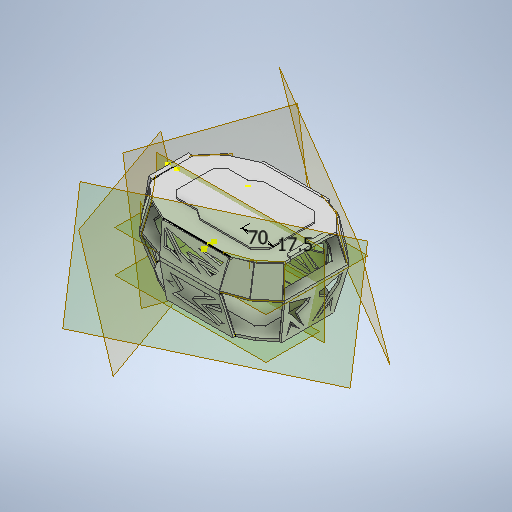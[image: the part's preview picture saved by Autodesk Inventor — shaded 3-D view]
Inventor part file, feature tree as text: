
AUTODESK INVENTOR PART (.ipt)
format: ipt  version: 2025.2 (Build 292293000, 293)  size: 6,053,888 bytes
history: native  units: mm
features: sketch x43, extrude x34, other x23, plane x17, loft x11, mirror x2
ambient origin geometry x8: Origin, YZ Plane, XZ Plane, XY Plane, X Axis, Y Axis, Z Axis, Center Point
bodies: Body1 (feature_tree)
feature tree (130):
  extrude  "Extrusion2"  Depth=45.0mm
  extrude  "Extrusion3"  Depth=40.0mm
  plane  "Work Plane3"
  extrude  "Extrusion4"  Depth=145.0mm
  extrude  "Extrusion5"  Depth=55.0mm
  plane  "Work Plane4"
  extrude  "Extrusion6"  Depth=40.0mm
  sketch  "Sketch8"  dims[d17=165.0deg d18=15.0mm]
  sketch  "Sketch9"  dims[d20=10.0mm d21=40.0mm]
  sketch  "Sketch10"  dims[d22=5.0mm d23=5.0mm]
  loft  "Loft1"
  loft  "Loft2"
  extrude  "Extrusion7"  Depth=5.0mm
  extrude  "Extrusion8"  TaperAngle=90.0deg  [1 undecoded]
  extrude  "Extrusion9"  Depth=30.0mm
  sketch  "Sketch14"  dims[d30=45.0mm d31=20.0mm]
  sketch  "Sketch15"  dims[d32=45.0deg d39=5.0mm d40=0.0mm]
  sketch  "Sketch16"  dims[d41=3.0mm d42=3.0mm d43=0.0mm d44=0.0mm d45=150.0mm]
  loft  "Loft3"
  loft  "Loft4"
  loft  "Loft5"
  extrude  "Extrusion10"  Depth=3.0mm
  extrude  "Extrusion11"  Depth=10.0mm
  extrude  "Extrusion12"  Depth=10.0mm
  extrude  "Extrusion13"  Depth=10.0mm
  extrude  "Extrusion14"  Depth=10.0mm
  loft  "Loft7"
  loft  "Loft8"
  sketch  "Sketch22"  dims[d57=10.0mm d58=10.0mm]
  plane  "Work Plane5"
  extrude  "Extrusion15"  Depth=3.0mm TaperAngle=0.0deg
  plane  "Work Plane6"
  extrude  "Extrusion16"  Depth=10.0mm
  extrude  "Extrusion17"  Depth=50.0mm
  plane  "Work Plane7"
  extrude  "Extrusion18"  Depth=50.0mm
  sketch  "Sketch28"  dims[d71=27.925268mm d72=10.0mm]
  extrude  "Extrusion19"  Depth=10.0mm
  extrude  "Extrusion20"  Depth=60.0mm
  extrude  "Extrusion21"  Depth=5.0mm TaperAngle=0.0deg
  extrude  "Extrusion22"  TaperAngle=0.0deg  [1 undecoded]
  extrude  "Extrusion23"  TaperAngle=0.0deg  [1 undecoded]
  extrude  "Extrusion24"  Depth=4.0mm TaperAngle=0.0deg
  extrude  "Extrusion25"  TaperAngle=0.0deg  [1 undecoded]
  extrude  "Extrusion26"  TaperAngle=0.0deg  [1 undecoded]
  extrude  "Extrusion27"  TaperAngle=0.0deg  [1 undecoded]
  plane  "Work Plane8"
  mirror  "Mirror1"
  loft  "Loft9"
  loft  "Loft10"
  loft  "Loft11"
  loft  "Loft12"
  plane  "Work Plane14"
  plane  "Work Plane15"
  extrude  "Extrusion28"  TaperAngle=0.0deg  [1 undecoded]
  extrude  "Extrusion29"  Depth=4.0mm TaperAngle=0.0deg
  plane  "Work Plane16"
  extrude  "Extrusion30"  Depth=92.689mm
  mirror  "Mirror2"
  extrude  "Extrusion31"  Depth=70.0mm
  sketch  "Sketch42"  dims[d126=4.0mm d127=0.0mm d128=4.0mm d129=0.0mm]
  extrude  "Extrusion32"  Depth=5.0mm
  extrude  "Extrusion33"  Depth=70.0mm
  extrude  "Extrusion34"  Depth=10.0mm
  extrude  "Extrusion35"  Depth=10.0mm
  sketch  "Sketch1"  dims[d6=115.0mm d8=45.0mm]
  other  "Image1"
  sketch  "Sketch3"  dims[d9=45.0deg d10=40.0mm]
  sketch  "Sketch4"  dims[d11=27.925268mm d12=145.0mm]
  sketch  "Sketch5"  dims[d13=27.052603mm d14=55.0mm]
  sketch  "Sketch6"  dims[d15=27.052603mm d16=40.0mm]
  other  "Edges1"
  other  "Edges2"
  other  "Edges3"
  other  "Edges4"
  sketch  "Sketch11"  dims[d24=40.0mm d25=90.0deg]
  sketch  "Sketch12"  dims[d26=30.0mm d27=110.0mm]
  sketch  "Sketch13"  dims[d28=25.0mm d29=25.307274mm]
  other  "Edges5"
  other  "Edges6"
  other  "Edges7"
  other  "Edges8"
  other  "Edges9"
  other  "Edges10"
  sketch  "Sketch17"  dims[d46=10.0mm d48=10.0mm]
  sketch  "Sketch18"  dims[d49=10.0mm d50=22.68928mm]
  sketch  "Sketch19"  dims[d51=10.0mm d52=10.0mm]
  sketch  "Sketch20"  dims[d53=10.0mm d54=10.0mm]
  sketch  "Sketch21"  dims[d55=10.0mm d56=10.0mm]
  other  "Edges13"
  other  "Edges14"
  other  "Edges15"
  other  "Edges16"
  sketch  "Sketch23"  dims[d59=5.0mm d60=0.0mm d61=3.0mm d62=3.0mm d63=0.0mm d64=0.0mm]
  sketch  "Sketch24"  dims[d65=-90.0mm d66=10.0mm]
  sketch  "Sketch25"  dims[d67=70.0mm d68=50.0mm]
  sketch  "Sketch26"  dims[d69=22.68928mm d70=50.0mm]
  sketch  "Sketch29"  dims[d73=50.0mm d74=60.0mm]
  sketch  "Sketch30"  dims[d75=70.0mm d76=5.0mm d77=0.0mm]
  sketch  "Sketch31"  dims[d78=0.0mm d79=90.0deg d80=0.0mm d81=90.0deg]
  sketch  "Sketch32"  dims[d82=0.0mm d83=90.0deg d84=0.0mm d85=90.0deg]
  sketch  "Sketch33"  dims[d86=4.0mm d87=0.0mm d88=4.0mm d89=0.0mm]
  sketch  "Sketch34"  dims[d90=4.0mm d91=0.0mm d92=0.0mm d93=90.0deg]
  sketch  "Sketch35"  dims[d94=0.0mm d95=90.0deg d96=0.0mm d97=90.0deg]
  sketch  "Sketch36"  dims[d98=0.0mm d99=90.0deg d100=0.0mm d101=90.0deg]
  sketch  "Sketch37"  dims[d102=0.0mm d103=90.0deg d104=4.0mm d105=0.0mm]
  plane  "Work Plane9"
  plane  "Work Plane10"
  plane  "Work Plane11"
  plane  "Work Plane12"
  plane  "Work Plane13"
  other  "Edges17"
  other  "Edges18"
  other  "Edges19"
  other  "Edges20"
  other  "Edges21"
  other  "Edges22"
  other  "Edges23"
  other  "Edges24"
  sketch  "Sketch38"  dims[d106=4.0mm d107=0.0mm d108=4.0mm d109=0.0mm]
  sketch  "Sketch39"  dims[d110=4.0mm d111=0.0mm d112=4.0mm d113=0.0mm]
  sketch  "Sketch40"  dims[d118=0.0mm d119=90.0deg d120=0.0mm d121=90.0deg]
  plane  "Work Plane17"
  plane  "Work Plane18"
  plane  "Work Plane19"
  sketch  "Sketch41"  dims[d122=0.0mm d123=90.0deg d124=0.0mm d125=90.0deg]
  sketch  "Sketch43"  dims[d130=4.0mm d131=0.0mm d132=92.689mm]
  sketch  "Sketch44"  dims[d133=4.0mm d134=0.0mm d135=70.0mm]
  sketch  "Sketch45"  dims[d136=17.5mm d137=5.0mm]
  sketch  "Sketch46"  dims[d138=25.0mm d139=70.0mm d140=25.0mm d141=17.5mm d142=90.0deg d143=23.0mm d144=0.0mm d145=70.0mm d146=3.0mm d147=17.5mm d148=0.0mm d149=25.0mm d150=30.0mm d151=15.0deg d152=90.0deg d153=5.0mm d154=20.0mm d155=90.0deg d156=4.363323mm d157=17.5mm d158=0.0mm d159=25.0mm d160=165.0deg d161=40.0mm d162=150.0deg d163=50.0mm d164=1.745329mm d165=40.0mm d166=5.0mm d167=40.0mm d168=30.543262mm d169=17.5mm d170=0.0mm d171=10.0mm d172=100.0mm d173=150.0deg d174=40.0mm d175=19.198622mm d176=100.0mm d177=70.0mm d178=30.0deg d179=100.0mm d180=10.0mm d181=10.0mm d182=10.0mm d183=4.363323mm d184=40.0mm d185=40.0mm d186=6.981317mm d187=20.0mm d188=24.43461mm d189=16.0mm d190=10.0mm d191=0.0mm d192=80.0mm d193=24.43461mm d194=120.0mm d195=30.0deg d196=40.0mm d197=30.0deg d198=50.0mm d199=10.0mm d200=50.0mm d201=55.0mm d202=1.745329mm d203=30.0mm d204=27.925268mm d205=40.0mm d206=5.0mm d207=30.0mm d208=30.0mm d209=17.453293mm d210=60.0mm d211=30.0mm d212=50.0mm d213=0.0mm d214=10.0mm d215=10.0mm d216=10.0mm d217=10.0mm d218=90.0deg d219=10.0mm d220=20.0mm d221=10.0mm d222=17.453293mm d223=25.0mm d224=22.68928mm d225=70.0mm d226=10.0mm d227=40.0mm d228=22.68928mm d229=20.0mm d230=75.0deg d231=50.0mm d232=0.0mm d233=5.0mm d234=0.0mm d235=5.0mm d236=0.0mm d238=0.0mm d239=90.0deg d240=0.0mm d241=90.0deg d242=0.0mm d243=90.0deg d244=0.0mm d245=90.0deg d246=0.0mm d247=90.0deg d248=0.0mm d249=90.0deg d250=0.0mm d251=90.0deg d252=0.0mm d253=90.0deg d254=3.0mm d255=0.0mm d256=3.0mm d257=0.0mm d258=3.0mm d259=0.0mm d260=30.0mm d261=50.0mm d262=90.0mm d263=30.0mm d264=5.0mm d265=0.0mm d266=20.0mm d267=100.0mm d268=20.0mm d269=100.0mm d270=30.0mm d271=40.0mm d272=30.0mm d273=5.0mm d274=5.0mm d275=0.0mm d276=0.0mm d277=10.0mm d278=10.0mm d279=30.0mm d280=0.0mm d281=20.0mm d282=20.0mm d283=20.0mm d284=90.0deg d285=10.0mm d286=0.0mm d287=20.0mm d288=100.0mm d289=0.0mm d290=10.0mm d291=10.0mm d292=10.0mm d293=0.0mm]
note: 7 required parameter values undecoded (feature->parameter linkage not recoverable at this tier; creation-order binding heuristic only, values carry confidence <= 0.55)
